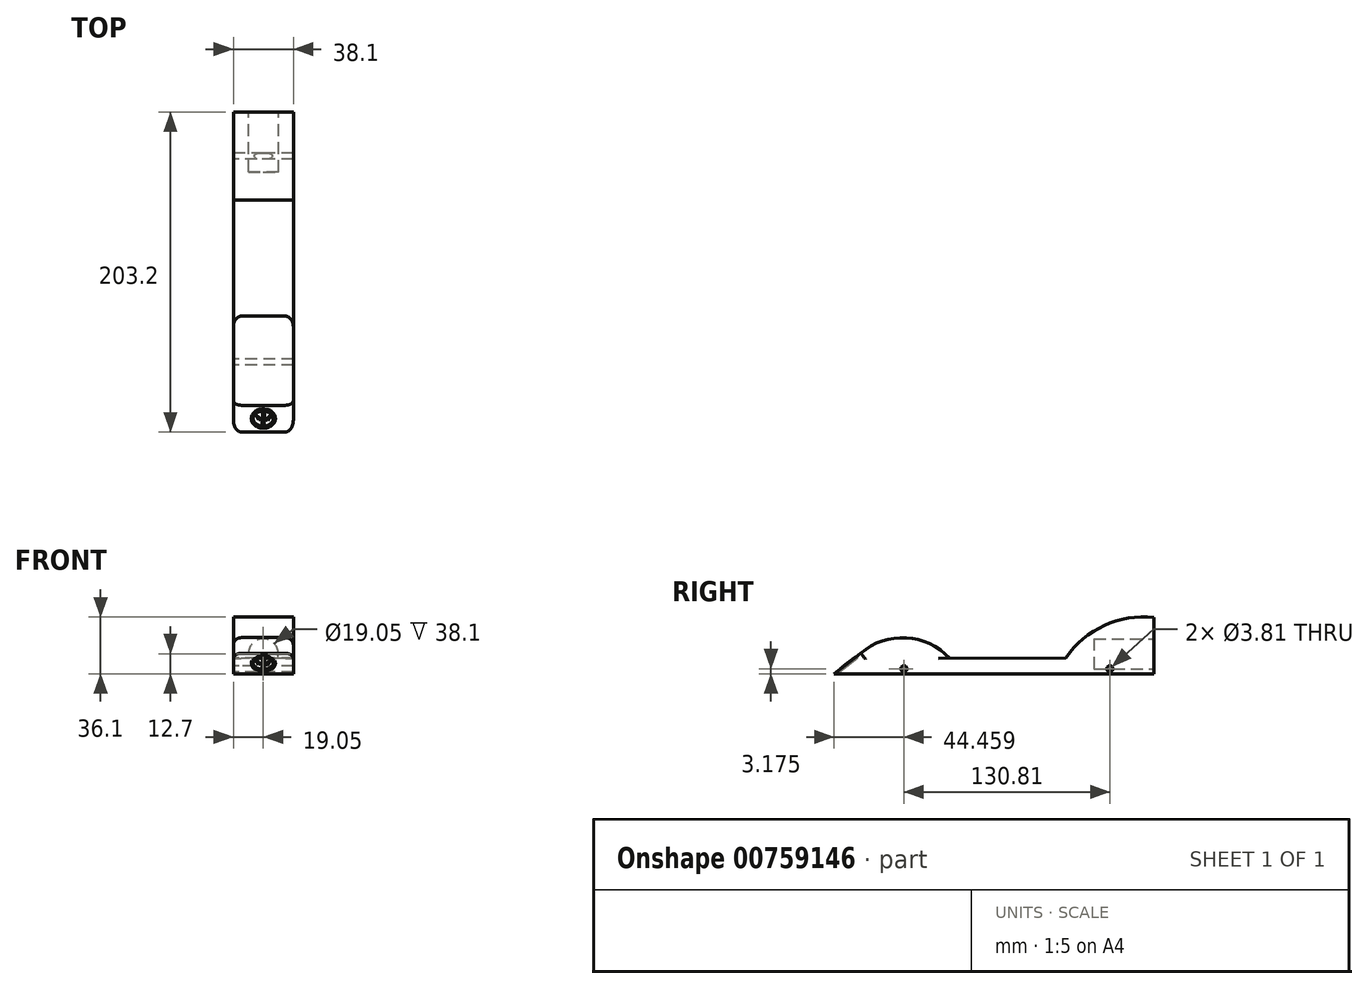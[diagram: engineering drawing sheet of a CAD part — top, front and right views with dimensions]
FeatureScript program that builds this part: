
annotation { "Feature Type Name" : "Feature", "Feature Type Description" : "" }
export const myFeature = defineFeature(function(context is Context, id is Id, definition is map)
    precondition{}
    {
        {
            var Q0;
            Q0=qCreatedBy(makeId("Right.planeOp"),FACE);
            var sketch = newSketch(context, id + "F0", { "sketchPlane" : qUnion([Q0])});
            skArc(sketch, "E0", {"start": v(-38.86, 9.88) * mm, "mid": v(-66.5, 22.88) * mm, "end": v(-95.44, 13.06) * mm});
            skLineSegment(sketch, "E1", {"start": v(-38.86, 9.88) * mm, "end": v(34.89, 10.2) * mm});
            skArc(sketch, "E2", {"start": v(90.79, 35.75) * mm, "mid": v(59.32, 30.67) * mm, "end": v(34.89, 10.2) * mm});
            skLineSegment(sketch, "E3", {"start": v(90.79, 35.75) * mm, "end": v(90.79, 0) * mm});
            skLineSegment(sketch, "E4", {"start": v(90.79, 0) * mm, "end": v(-112.41, 0) * mm});
            skLineSegment(sketch, "E5", {"start": v(-95.44, 13.06) * mm, "end": v(-112.41, 0) * mm});
            skSolve(sketch);
        }
        {
            var Q0;
            Q0 = qSketchRegion(id + "F0", true);
            extrude(context, id + "F1", {"entities" : qUnion([Q0]), "depth" : 19.05 * mm, "offsetDistance" : 25.4 * mm, "hasSecondDirection" : true, "secondDirectionOppositeDirection" : true, "secondDirectionDepth" : 19.05 * mm});
        }
        {
            var Q0;
            Q0=makeQuery(id+"F1.opExtrude","SWEPT_FACE",FACE,{"disambiguationData":[OSD([sQuery(id+"F0.wireOp",EDGE,"E5")])]});
            var sketch = newSketch(context, id + "F2", { "sketchPlane" : qUnion([Q0])});
            skCircle(sketch, "E6", {"center": v(0, -34.98) * mm, "radius": 4.1 * mm});
            skArc(sketch, "E7", {"start": v(-0.74, -33.1) * mm, "mid": v(-3.02, -35) * mm, "end": v(-0.7, -36.85) * mm});
            skArc(sketch, "E8", {"start": v(1.05, -37.03) * mm, "mid": v(3.07, -35.01) * mm, "end": v(0.97, -33.08) * mm});
            skLineSegment(sketch, "E9", {"start": v(-0.74, -33.1) * mm, "end": v(-0.7, -36.85) * mm});
            skLineSegment(sketch, "E10", {"start": v(0.97, -33.08) * mm, "end": v(1.05, -37.03) * mm});
            skSolve(sketch);
        }
        {
            var Q0;
            Q0 = qSketchRegion(id + "F2", true);
            extrude(context, id + "F3", {"entities" : qUnion([Q0]), "operationType" : NewBodyOperationType.REMOVE, "oppositeDirection" : true, "depth" : 0.23 * mm, "offsetDistance" : 25.4 * mm});
        }
        {
            var Q0;
            Q0=makeQuery(id+"F1.opExtrude","SWEPT_FACE",FACE,{"disambiguationData":[OSD([sQuery(id+"F0.wireOp",EDGE,"E3")])]});
            var sketch = newSketch(context, id + "F4", { "sketchPlane" : qUnion([Q0])});
            skCircle(sketch, "E11", {"center": v(0, 12.7) * mm, "radius": 9.53 * mm});
            skSolve(sketch);
        }
        {
            var Q0;
            Q0 = qSketchRegion(id + "F4", true);
            extrude(context, id + "F5", {"entities" : qUnion([Q0]), "operationType" : NewBodyOperationType.REMOVE, "oppositeDirection" : true, "depth" : 38.1 * mm, "offsetDistance" : 25.4 * mm});
        }
        {
            var Q0;
            Q0=makeQuery(id+"F1.opExtrude","SWEPT_FACE",FACE,{"disambiguationData":[OSD([sQuery(id+"F0.wireOp",EDGE,"E5")])]});
            var sketch = newSketch(context, id + "F6", { "sketchPlane" : qUnion([Q0])});
            skCircle(sketch, "E12", {"center": v(0, -78.42) * mm, "radius": 7.65 * mm});
            skSolve(sketch);
        }
        {
            var Q0;
            Q0=makeQuery(id+"F6.imprint","IMPRINT",FACE,{"disambiguationData":[TD([[makeQuery(id+"F6.imprint","IMPRINT",EDGE,{"derivedFrom":sQuery(id+"F6.wireOp",EDGE,"E12")}),1.0]])]});
            extrude(context, id + "F7", {"entities" : qUnion([Q0]), "operationType" : NewBodyOperationType.REMOVE, "oppositeDirection" : true, "depth" : 1.27 * mm, "offsetDistance" : 25.4 * mm});
        }
        {
            var Q0;
            Q0=makeQuery(id+"F7.boolean.opBoolean","COPY",FACE,{"derivedFrom":makeQuery(id+"F7.opExtrude","CAP_FACE",FACE,{"disambiguationData":[OSD([sQuery(id+"F6.wireOp",EDGE,"E12")])],"isStart":false})});
            var sketch = newSketch(context, id + "F8", { "sketchPlane" : qUnion([Q0])});
            skArc(sketch, "E13", {"start": v(-0.43, -72.33) * mm, "mid": v(-6.43, -78.22) * mm, "end": v(-0.71, -84.38) * mm});
            skLineSegment(sketch, "E14", {"start": v(-0.43, -72.33) * mm, "end": v(-0.71, -84.38) * mm});
            skArc(sketch, "E15", {"start": v(0.4, -84.56) * mm, "mid": v(6.18, -78.53) * mm, "end": v(0.68, -72.25) * mm});
            skLineSegment(sketch, "E16", {"start": v(0.68, -72.25) * mm, "end": v(0.4, -84.56) * mm});
            skSolve(sketch);
        }
        {
            var Q0;
            Q0 = qSketchRegion(id + "F8", true);
            extrude(context, id + "F9", {"entities" : qUnion([Q0]), "operationType" : NewBodyOperationType.ADD, "depth" : 1.4 * mm, "offsetDistance" : 25.4 * mm});
        }
        {
            var Q0;
            Q0=makeQuery(id+"F9.opExtrude","CAP_FACE",FACE,{"disambiguationData":[OSD([sQuery(id+"F8.wireOp",EDGE,"E13"),sQuery(id+"F8.wireOp",EDGE,"E14")])],"isStart":false});
            var sketch = newSketch(context, id + "F10", { "sketchPlane" : qUnion([Q0])});
            skLineSegment(sketch, "E17", {"start": v(-4.53, -75.46) * mm, "end": v(-1.6, -78.73) * mm});
            skLineSegment(sketch, "E18", {"start": v(-1.6, -78.73) * mm, "end": v(-3.1, -79.53) * mm});
            skLineSegment(sketch, "E19", {"start": v(-3.1, -79.53) * mm, "end": v(-4.53, -75.46) * mm});
            skLineSegment(sketch, "E20", {"start": v(1.32, -79) * mm, "end": v(4.58, -75.86) * mm});
            skLineSegment(sketch, "E21", {"start": v(4.58, -75.86) * mm, "end": v(2.82, -79.8) * mm});
            skLineSegment(sketch, "E22", {"start": v(2.82, -79.8) * mm, "end": v(1.32, -79) * mm});
            skSolve(sketch);
        }
        {
            var Q0;
            Q0 = qSketchRegion(id + "F10", true);
            extrude(context, id + "F11", {"entities" : qUnion([Q0]), "operationType" : NewBodyOperationType.REMOVE, "oppositeDirection" : true, "depth" : 0.38 * mm, "offsetDistance" : 25.4 * mm});
        }
        {
            var Q0;
            Q0=makeQuery(id+"F1.opExtrude","CAP_EDGE",EDGE,{"disambiguationData":[OSD([sQuery(id+"F0.wireOp",EDGE,"E0")])],"isStart":false});
            var Q1;
            Q1=makeQuery(id+"F1.opExtrude","CAP_EDGE",EDGE,{"disambiguationData":[OSD([sQuery(id+"F0.wireOp",EDGE,"E0")])],"isStart":true});
            fillet(context, id + "F12", {"entities" : qUnion([Q0, Q1]), "radius" : 4.9 * mm, "tangentPropagation" : true, "allowEdgeOverflow" : false});
        }
        {
            var Q0;
            Q0=makeQuery(id+"F1.opExtrude","CAP_FACE",FACE,{"disambiguationData":[OSD([sQuery(id+"F0.wireOp",EDGE,"E0"),sQuery(id+"F0.wireOp",EDGE,"E1"),sQuery(id+"F0.wireOp",EDGE,"E2"),sQuery(id+"F0.wireOp",EDGE,"E3"),sQuery(id+"F0.wireOp",EDGE,"E4"),sQuery(id+"F0.wireOp",EDGE,"E5")])],"isStart":true});
            var sketch = newSketch(context, id + "F13", { "sketchPlane" : qUnion([Q0])});
            skCircle(sketch, "E23", {"center": v(67.95, 3.18) * mm, "radius": 1.9 * mm});
            skCircle(sketch, "E24", {"center": v(-62.86, 3.18) * mm, "radius": 1.9 * mm});
            skSolve(sketch);
        }
        {
            var Q0;
            Q0 = qSketchRegion(id + "F13", true);
            extrude(context, id + "F14", {"entities" : qUnion([Q0]), "operationType" : NewBodyOperationType.REMOVE, "oppositeDirection" : true, "depth" : 49.78 * mm, "offsetDistance" : 25.4 * mm});
        }
    });
